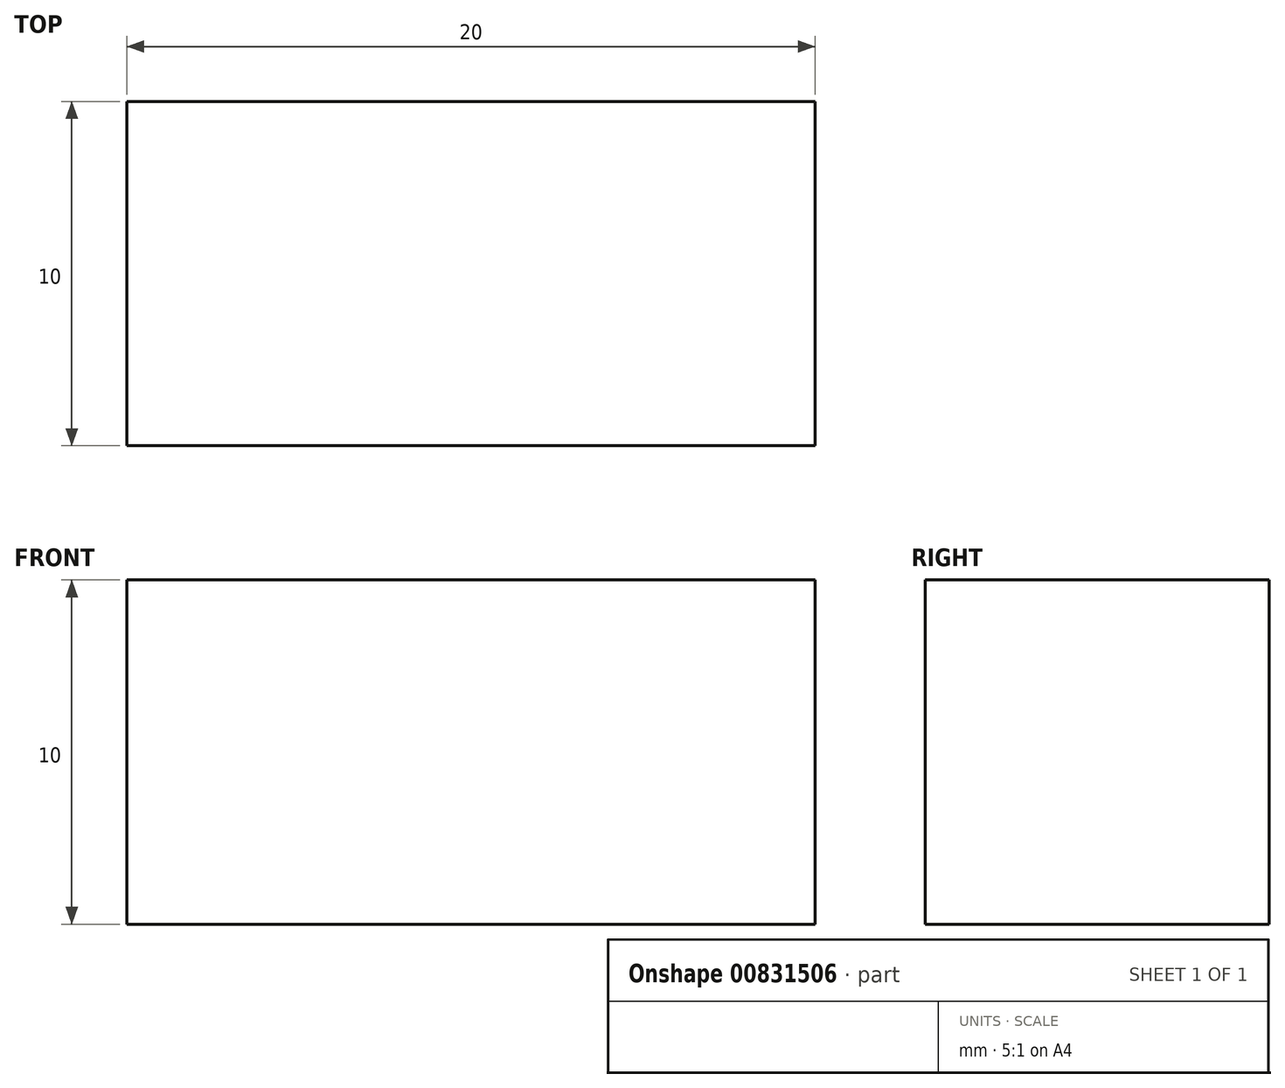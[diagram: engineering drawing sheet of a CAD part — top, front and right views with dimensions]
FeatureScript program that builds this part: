
annotation { "Feature Type Name" : "Feature", "Feature Type Description" : "" }
export const myFeature = defineFeature(function(context is Context, id is Id, definition is map)
    precondition{}
    {
        {
            var Q0;
            Q0=qCreatedBy(makeId("Top.planeOp"),FACE);
            var sketch = newSketch(context, id + "F0", { "sketchPlane" : qUnion([Q0])});
            skLineSegment(sketch, "E0.bottom", {"start": v(-10, 5) * mm, "end": v(10, 5) * mm});
            skLineSegment(sketch, "E0.top", {"start": v(-10, -5) * mm, "end": v(10, -5) * mm});
            skLineSegment(sketch, "E0.left", {"start": v(-10, 5) * mm, "end": v(-10, -5) * mm});
            skLineSegment(sketch, "E0.right", {"start": v(10, 5) * mm, "end": v(10, -5) * mm});
            skSolve(sketch);
        }
        {
            var Q0;
            Q0=makeQuery(id+"F0.imprint","IMPRINT",FACE,{"disambiguationData":[TD([[makeQuery(id+"F0.imprint","IMPRINT",EDGE,{"derivedFrom":sQuery(id+"F0.wireOp",EDGE,"E0.bottom")}),-1.0]])]});
            extrude(context, id + "F1", {"entities" : qUnion([Q0]), "depth" : 10 * mm, "offsetDistance" : 25 * mm});
        }
    });
